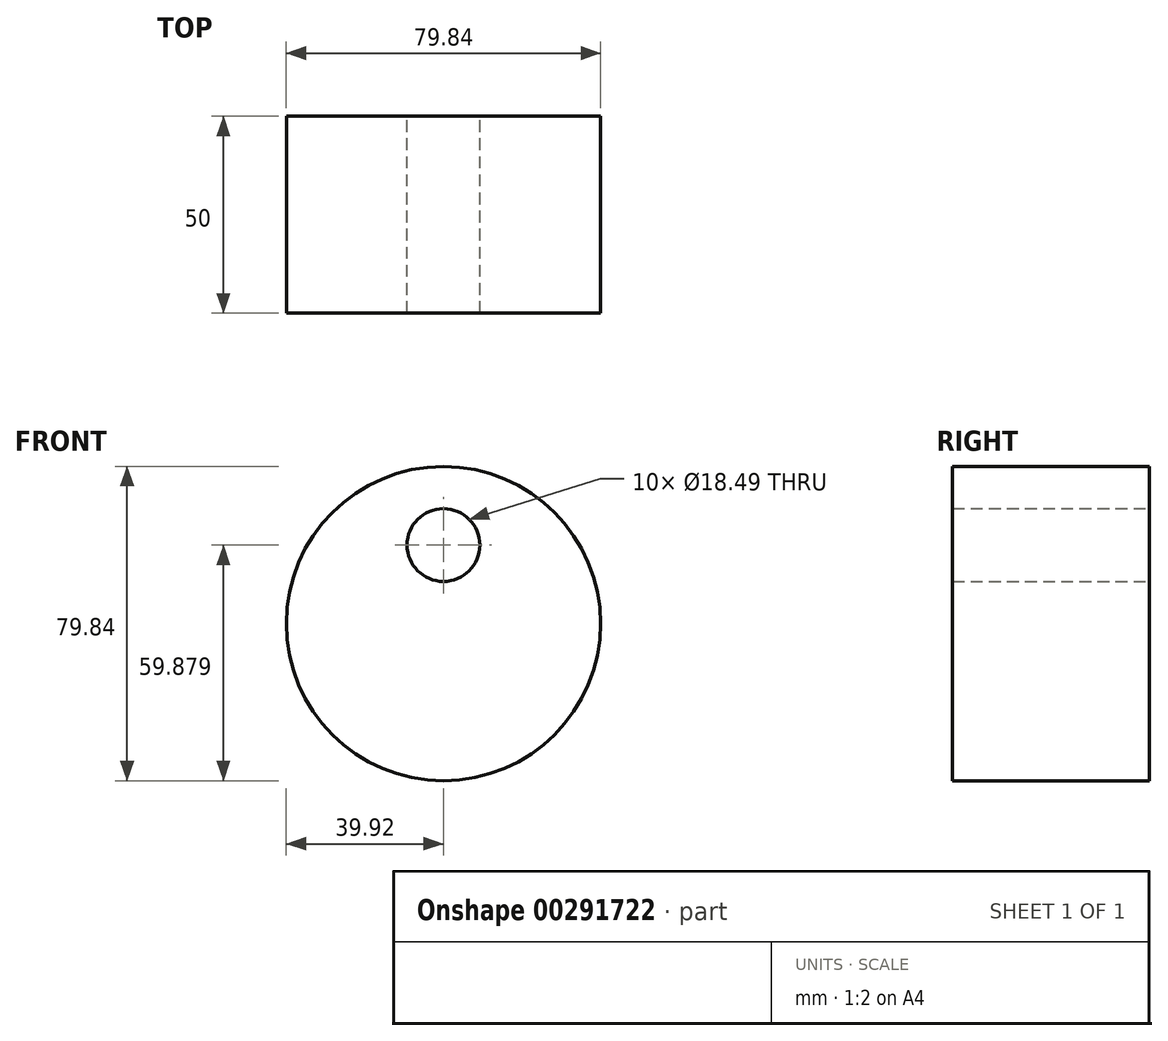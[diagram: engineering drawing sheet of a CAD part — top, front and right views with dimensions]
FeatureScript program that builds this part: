
annotation { "Feature Type Name" : "Feature", "Feature Type Description" : "" }
export const myFeature = defineFeature(function(context is Context, id is Id, definition is map)
    precondition{}
    {
        {
            var Q0;
            Q0=qCreatedBy(makeId("Front.planeOp"),FACE);
            var sketch = newSketch(context, id + "F0", { "sketchPlane" : qUnion([Q0])});
            skCircle(sketch, "E0", {"center": v(0, 0) * mm, "radius": 39.92 * mm});
            skCircle(sketch, "E1", {"center": v(0, 19.96) * mm, "radius": 9.24 * mm});
            skSolve(sketch);
        }
        {
            var Q0;
            Q0=makeQuery(id+"F0.imprint","IMPRINT",FACE,{"disambiguationData":[TD([[makeQuery(id+"F0.imprint","IMPRINT",EDGE,{"derivedFrom":sQuery(id+"F0.wireOp",EDGE,"E0")}),1.0]])]});
            extrude(context, id + "F1", {"entities" : qUnion([Q0]), "depth" : 50 * mm});
        }
    });
